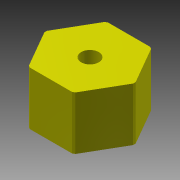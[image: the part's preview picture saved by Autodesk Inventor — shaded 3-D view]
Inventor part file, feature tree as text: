
AUTODESK INVENTOR PART (.ipt)
format: ipt  version: 2013 (Build 170138000, 138)  size: 229,376 bytes
history: native  units: mm
features: sketch x7, extrude x6, helix x1, projected_geometry x1
ambient origin geometry x8: Origin, YZ Plane, XZ Plane, XY Plane, X Axis, Y Axis, Z Axis, Center Point
bodies: Solid1 (feature_tree)
feature tree (15):
  extrude  "Extrusion1"  Depth=15.0mm TaperAngle=0.0deg
  extrude  "Extrusion2"  Depth=15.0mm TaperAngle=0.0deg
  helix  "Coil1"  [1 undecoded]
  extrude  "Extrusion8"  Depth=5.0mm TaperAngle=0.0deg
  extrude  "Extrusion9"  Depth=5.0mm
  extrude  "Extrusion10"  Depth=22.0mm
  extrude  "Extrusion11"  [1 undecoded]
  sketch  "Sketch1"  dims[d0=25.0mm d2=15.0mm d3=0.0mm]
  sketch  "Sketch2"  dims[d4=13.9mm d9=15.0mm d10=0.0mm d11=2.0mm]
  sketch  "Sketch3"  dims[d12=2.0001mm d13=10.0mm d14=100.0mm d15=0.0mm d16=90.0deg d17=90.0deg d18=0.0mm d19=0.0mm d47=5.0mm d48=0.0mm]
  sketch  "Sketch9"  dims[d49=5.0mm d50=-7.853982mm d51=5.0mm]
  sketch  "Sketch10"  dims[d53=5.0mm d54=0.0mm d55=22.0mm]
  sketch  "Sketch11"  dims[d56=0.0mm d57=0.0mm]
  sketch  "Sketch12"
  projected_geometry  "Project Cut Edges1"
note: 2 required parameter values undecoded (feature->parameter linkage not recoverable at this tier; creation-order binding heuristic only, values carry confidence <= 0.55)
